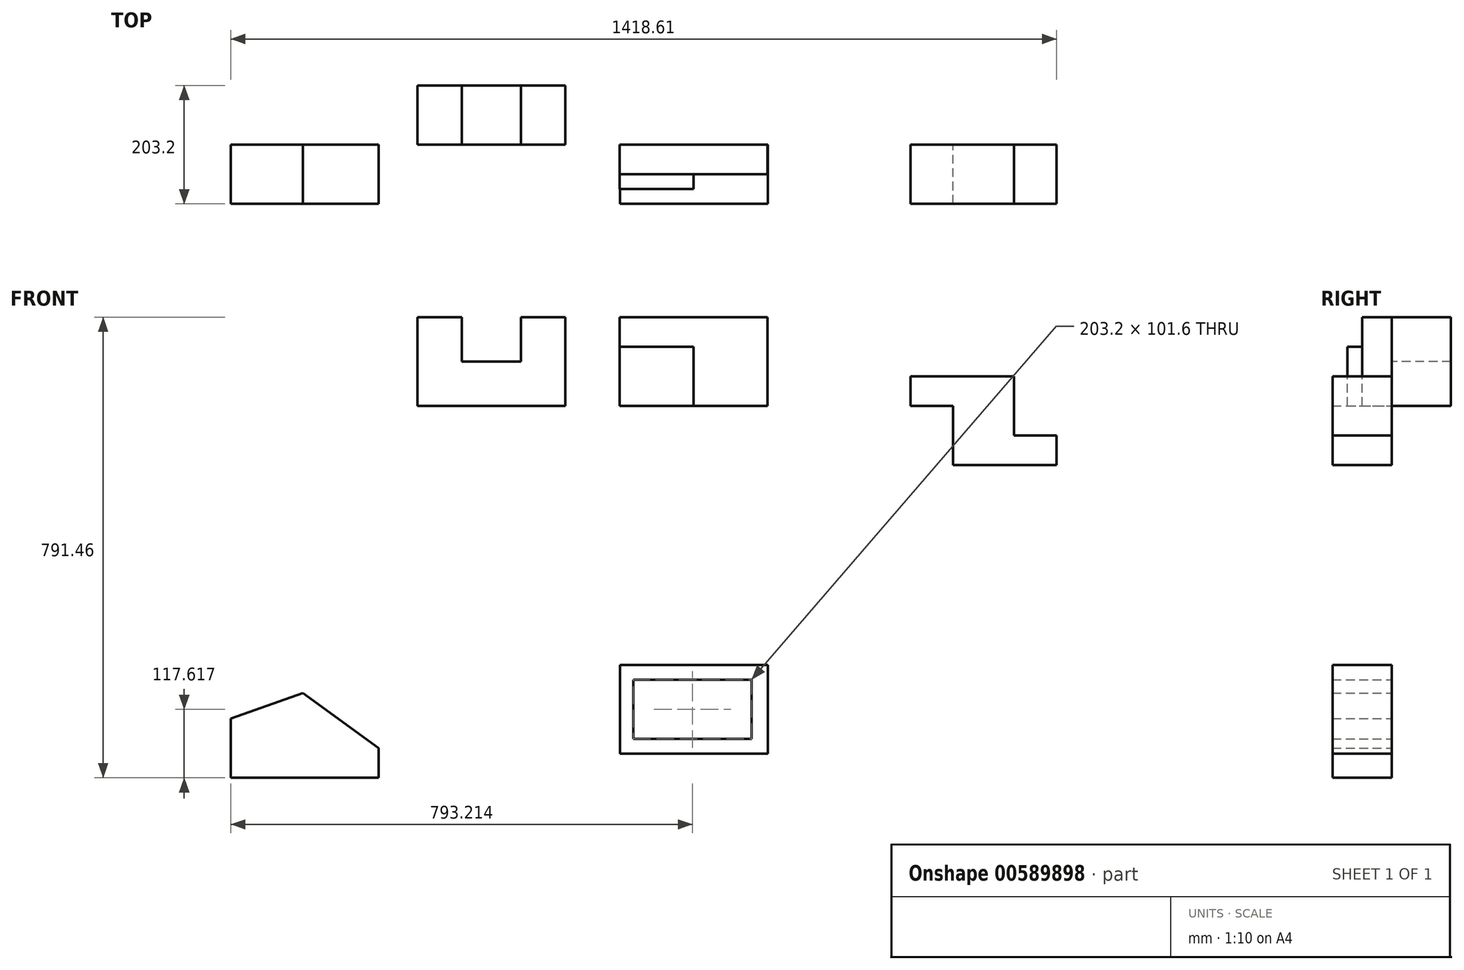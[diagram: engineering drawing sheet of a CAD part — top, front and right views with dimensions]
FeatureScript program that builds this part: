
annotation { "Feature Type Name" : "Feature", "Feature Type Description" : "" }
export const myFeature = defineFeature(function(context is Context, id is Id, definition is map)
    precondition{}
    {
        {
            var Q0;
            Q0=qCreatedBy(makeId("Front.planeOp"),FACE);
            var sketch = newSketch(context, id + "F0", { "sketchPlane" : qUnion([Q0])});
            skLineSegment(sketch, "E0", {"start": v(254, 152.4) * mm, "end": v(254, 0) * mm});
            skLineSegment(sketch, "E1", {"start": v(0, 0) * mm, "end": v(254, 0) * mm});
            skLineSegment(sketch, "E2", {"start": v(254, 152.4) * mm, "end": v(177.8, 152.4) * mm});
            skLineSegment(sketch, "E3", {"start": v(177.8, 76.2) * mm, "end": v(76.2, 76.2) * mm});
            skLineSegment(sketch, "E4", {"start": v(76.2, 76.2) * mm, "end": v(76.2, 152.4) * mm});
            skLineSegment(sketch, "E5", {"start": v(177.8, 76.2) * mm, "end": v(177.8, 152.4) * mm});
            skLineSegment(sketch, "E6", {"start": v(76.2, 152.4) * mm, "end": v(0, 152.4) * mm});
            skLineSegment(sketch, "E7", {"start": v(0, 0) * mm, "end": v(0, 152.4) * mm});
            skSolve(sketch);
        }
        {
            var Q0;
            Q0=makeQuery(id+"F0.imprint","IMPRINT",FACE,{"disambiguationData":[TD([[makeQuery(id+"F0.imprint","IMPRINT",EDGE,{"derivedFrom":sQuery(id+"F0.wireOp",EDGE,"E0")}),-1.0]])]});
            extrude(context, id + "F1", {"entities" : qUnion([Q0]), "oppositeDirection" : true, "depth" : 101.6 * mm, "offsetDistance" : 25.4 * mm});
        }
        {
            var Q0;
            Q0=qCreatedBy(makeId("Front.planeOp"),FACE);
            var sketch = newSketch(context, id + "F2", { "sketchPlane" : qUnion([Q0])});
            skLineSegment(sketch, "E8.bottom", {"start": v(601.12, 0) * mm, "end": v(347.12, 0) * mm});
            skLineSegment(sketch, "E8.top", {"start": v(601.12, 152.4) * mm, "end": v(347.12, 152.4) * mm});
            skLineSegment(sketch, "E8.left", {"start": v(601.12, 0) * mm, "end": v(601.12, 152.4) * mm});
            skLineSegment(sketch, "E8.right", {"start": v(347.12, 0) * mm, "end": v(347.12, 152.4) * mm});
            skSolve(sketch);
        }
        {
            var Q0;
            Q0=qSketchRegion(id+"F2",true);
            extrude(context, id + "F3", {"entities" : qUnion([Q0]), "depth" : 101.6 * mm, "offsetDistance" : 25.4 * mm});
        }
        {
            var Q0;
            Q0=makeQuery(id+"F3.opExtrude","SWEPT_FACE",FACE,{"disambiguationData":[OSD([sQuery(id+"F2.wireOp",EDGE,"E8.top")])]});
            var sketch = newSketch(context, id + "F4", { "sketchPlane" : qUnion([Q0])});
            skLineSegment(sketch, "E9.bottom", {"start": v(601.12, -101.6) * mm, "end": v(474.12, -101.6) * mm});
            skLineSegment(sketch, "E9.top", {"start": v(601.12, -50.8) * mm, "end": v(474.12, -50.8) * mm});
            skLineSegment(sketch, "E9.left", {"start": v(601.12, -101.6) * mm, "end": v(601.12, -50.8) * mm});
            skLineSegment(sketch, "E9.right", {"start": v(474.12, -101.6) * mm, "end": v(474.12, -50.8) * mm});
            skSolve(sketch);
        }
        {
            var Q0;
            Q0=makeQuery(id+"F4.imprint","IMPRINT",FACE,{"disambiguationData":[TD([[makeQuery(id+"F4.imprint","IMPRINT",EDGE,{"derivedFrom":sQuery(id+"F4.wireOp",EDGE,"E9.bottom")}),-1.0]])]});
            extrude(context, id + "F5", {"entities" : qUnion([Q0]), "operationType" : NewBodyOperationType.REMOVE, "oppositeDirection" : true, "depth" : 152.4 * mm, "offsetDistance" : 25.4 * mm});
        }
        {
            var Q0;
            Q0=makeQuery(id+"F3.opExtrude","CAP_FACE",FACE,{"disambiguationData":[OSD([sQuery(id+"F2.wireOp",EDGE,"E8.bottom"),sQuery(id+"F2.wireOp",EDGE,"E8.top"),sQuery(id+"F2.wireOp",EDGE,"E8.left"),sQuery(id+"F2.wireOp",EDGE,"E8.right")])],"isStart":false});
            var sketch = newSketch(context, id + "F6", { "sketchPlane" : qUnion([Q0])});
            skLineSegment(sketch, "E10.bottom", {"start": v(347.12, 152.4) * mm, "end": v(474.12, 152.4) * mm});
            skLineSegment(sketch, "E10.top", {"start": v(347.12, 50.8) * mm, "end": v(474.12, 50.8) * mm});
            skLineSegment(sketch, "E10.left", {"start": v(347.12, 152.4) * mm, "end": v(347.12, 50.8) * mm});
            skLineSegment(sketch, "E10.right", {"start": v(474.12, 152.4) * mm, "end": v(474.12, 50.8) * mm});
            skSolve(sketch);
        }
        {
            var Q0;
            Q0=makeQuery(id+"F6.imprint","IMPRINT",FACE,{"disambiguationData":[TD([[makeQuery(id+"F6.imprint","IMPRINT",EDGE,{"derivedFrom":sQuery(id+"F6.wireOp",EDGE,"E10.bottom")}),1.0]])]});
            extrude(context, id + "F7", {"entities" : qUnion([Q0]), "operationType" : NewBodyOperationType.REMOVE, "oppositeDirection" : true, "depth" : 25.4 * mm, "offsetDistance" : 25.4 * mm});
        }
        {
            var Q0;
            Q0=makeQuery(id+"F7.boolean.opBoolean","COPY",FACE,{"derivedFrom":makeQuery(id+"F7.opExtrude","SWEPT_FACE",FACE,{"disambiguationData":[OSD([sQuery(id+"F6.wireOp",EDGE,"E10.top")])]})});
            extrude(context, id + "F8", {"entities" : qUnion([Q0]), "operationType" : NewBodyOperationType.ADD, "depth" : 50.8 * mm, "offsetDistance" : 25.4 * mm});
        }
        {
            var Q0;
            Q0=makeQuery(id+"F8.opExtrude","CAP_FACE",FACE,{"disambiguationData":[OSD([sQuery(id+"F6.wireOp",EDGE,"E10.top")])],"isStart":false});
            extrude(context, id + "F9", {"entities" : qUnion([Q0]), "operationType" : NewBodyOperationType.REMOVE, "oppositeDirection" : true, "depth" : 25.4 * mm, "offsetDistance" : 25.4 * mm});
        }
        {
            var Q0;
            Q0=makeQuery(id+"F9.boolean.opBoolean","COPY",FACE,{"derivedFrom":makeQuery(id+"F9.opExtrude","CAP_FACE",FACE,{"disambiguationData":[OSD([sQuery(id+"F6.wireOp",EDGE,"E10.top")])],"isStart":false})});
            extrude(context, id + "F10", {"entities" : qUnion([Q0]), "operationType" : NewBodyOperationType.REMOVE, "oppositeDirection" : true, "depth" : 76.2 * mm, "offsetDistance" : 25.4 * mm});
        }
        {
            var Q0;
            Q0=makeQuery(id+"F3.opExtrude","SWEPT_FACE",FACE,{"disambiguationData":[OSD([sQuery(id+"F2.wireOp",EDGE,"E8.top")])]});
            var sketch = newSketch(context, id + "F11", { "sketchPlane" : qUnion([Q0])});
            skLineSegment(sketch, "E11.bottom", {"start": v(474.12, -50.8) * mm, "end": v(347.12, -50.8) * mm});
            skLineSegment(sketch, "E11.top", {"start": v(474.12, -76.2) * mm, "end": v(347.12, -76.2) * mm});
            skLineSegment(sketch, "E11.left", {"start": v(474.12, -50.8) * mm, "end": v(474.12, -76.2) * mm});
            skLineSegment(sketch, "E11.right", {"start": v(347.12, -50.8) * mm, "end": v(347.12, -76.2) * mm});
            skSolve(sketch);
        }
        {
            var Q0;
            Q0=qSketchRegion(id+"F11",true);
            extrude(context, id + "F12", {"entities" : qUnion([Q0]), "operationType" : NewBodyOperationType.REMOVE, "oppositeDirection" : true, "depth" : 50.8 * mm, "offsetDistance" : 25.4 * mm});
        }
        {
            var Q0;
            Q0=qCreatedBy(makeId("Front.planeOp"),FACE);
            var sketch = newSketch(context, id + "F13", { "sketchPlane" : qUnion([Q0])});
            skLineSegment(sketch, "E12", {"start": v(1097.77, -101.6) * mm, "end": v(1097.77, -50.8) * mm});
            skLineSegment(sketch, "E13", {"start": v(919.97, -101.56) * mm, "end": v(1097.77, -101.6) * mm});
            skLineSegment(sketch, "E14", {"start": v(1097.77, -50.8) * mm, "end": v(1024.56, -50.8) * mm});
            skLineSegment(sketch, "E15", {"start": v(1024.56, -50.8) * mm, "end": v(1024.56, 50.8) * mm});
            skLineSegment(sketch, "E16", {"start": v(1024.56, 50.8) * mm, "end": v(846.76, 50.8) * mm});
            skLineSegment(sketch, "E17", {"start": v(846.76, 50.8) * mm, "end": v(846.76, 0) * mm});
            skLineSegment(sketch, "E18", {"start": v(919.97, -101.56) * mm, "end": v(919.97, 0) * mm});
            skLineSegment(sketch, "E19", {"start": v(846.76, 0) * mm, "end": v(919.97, 0) * mm});
            skSolve(sketch);
        }
        {
            var Q0;
            Q0=qSketchRegion(id+"F13",true);
            extrude(context, id + "F14", {"entities" : qUnion([Q0]), "depth" : 101.6 * mm, "offsetDistance" : 25.4 * mm});
        }
        {
            var Q0;
            Q0=qCreatedBy(makeId("Front.planeOp"),FACE);
            var sketch = newSketch(context, id + "F15", { "sketchPlane" : qUnion([Q0])});
            skLineSegment(sketch, "E20", {"start": v(-66.84, -639.06) * mm, "end": v(-66.84, -588.26) * mm});
            skLineSegment(sketch, "E21", {"start": v(-320.84, -537.46) * mm, "end": v(-320.84, -639.06) * mm});
            skLineSegment(sketch, "E22", {"start": v(-66.84, -639.06) * mm, "end": v(-320.84, -639.06) * mm});
            skLineSegment(sketch, "E23", {"start": v(-320.84, -537.46) * mm, "end": v(-197.2, -493.3) * mm});
            skLineSegment(sketch, "E24", {"start": v(-197.2, -493.3) * mm, "end": v(-66.84, -588.26) * mm});
            skSolve(sketch);
        }
        {
            var Q0;
            Q0=qSketchRegion(id+"F15",true);
            extrude(context, id + "F16", {"entities" : qUnion([Q0]), "depth" : 101.6 * mm, "offsetDistance" : 25.4 * mm});
        }
        {
            var Q0;
            Q0=qCreatedBy(makeId("Front.planeOp"),FACE);
            var sketch = newSketch(context, id + "F17", { "sketchPlane" : qUnion([Q0])});
            skLineSegment(sketch, "E25", {"start": v(602.16, -597.64) * mm, "end": v(602.16, -445.24) * mm});
            skLineSegment(sketch, "E26", {"start": v(602.16, -445.24) * mm, "end": v(348.16, -445.24) * mm});
            skLineSegment(sketch, "E27", {"start": v(348.16, -445.24) * mm, "end": v(348.16, -597.64) * mm});
            skLineSegment(sketch, "E28", {"start": v(348.16, -597.64) * mm, "end": v(602.16, -597.64) * mm});
            skLineSegment(sketch, "E29", {"start": v(370.77, -572.24) * mm, "end": v(370.77, -470.64) * mm});
            skLineSegment(sketch, "E30", {"start": v(370.77, -470.64) * mm, "end": v(573.97, -470.64) * mm});
            skLineSegment(sketch, "E31", {"start": v(573.97, -470.64) * mm, "end": v(573.97, -572.24) * mm});
            skLineSegment(sketch, "E32", {"start": v(370.77, -572.24) * mm, "end": v(573.97, -572.24) * mm});
            skSolve(sketch);
        }
        {
            var Q0;
            Q0=qSketchRegion(id+"F17",true);
            extrude(context, id + "F18", {"entities" : qUnion([Q0]), "depth" : 101.6 * mm, "offsetDistance" : 25.4 * mm});
        }
    });
